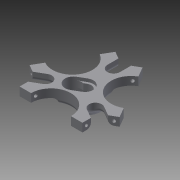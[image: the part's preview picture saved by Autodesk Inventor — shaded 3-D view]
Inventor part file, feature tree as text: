
AUTODESK INVENTOR PART (.ipt)
format: ipt  version: 2015 SP1 (Build 190203100, 203)  size: 376,320 bytes
history: native  units: mm
features: sketch x7, extrude x6, hole x1, pattern_circular x1, fillet x1
ambient origin geometry x8: Origin, YZ Plane, XZ Plane, XY Plane, X Axis, Y Axis, Z Axis, Center Point
bodies: Body1 (feature_tree)
feature tree (16):
  extrude  "Extrusion2"  Depth=60.0mm
  extrude  "Extrusion3"  Depth=60.0mm
  extrude  "Extrusion4"  Depth=13.0mm TaperAngle=0.0deg
  extrude  "Extrusion5"  Depth=4.0mm TaperAngle=0.0deg
  extrude  "Extrusion6"  Depth=4.0mm TaperAngle=0.0deg
  hole  "Hole1"  [1 undecoded]
  pattern_circular  "Circular Pattern1"  Count=3 Angle=360.0deg
  extrude  "Extrusion8"  Depth=4.0mm TaperAngle=360.0deg
  fillet  "Fillet2"  Radius=34.0mm
  sketch  "Sketch1"  dims[d2=15.0mm d3=60.0mm]
  sketch  "Sketch2"  dims[d7=19.05mm d8=60.0mm]
  sketch  "Sketch3"  dims[d10=12.0mm d11=13.0mm d12=0.0mm]
  sketch  "Sketch4"  dims[d13=16.0mm d14=4.0mm d15=0.0mm]
  sketch  "Sketch5"  dims[d16=3.0mm d17=0.0mm d18=4.0mm d19=0.0mm]
  sketch  "Sketch6"  dims[d20=12.0mm d23=55.0mm d24=30.0mm d26=360.0deg]
  sketch  "Sketch8"  dims[d28=4.0mm d29=0.0mm d30=3.0mm d31=6.0mm d32=4.0mm d33=2.0mm d34=90.0deg d35=8.0mm d36=20.594885mm d37=30.0mm d38=360.0deg d40=34.0mm d43=100.0mm d44=5.0mm d45=-5.235988mm d46=4.0mm]
note: 1 required parameter value undecoded (feature->parameter linkage not recoverable at this tier; creation-order binding heuristic only, values carry confidence <= 0.55)
